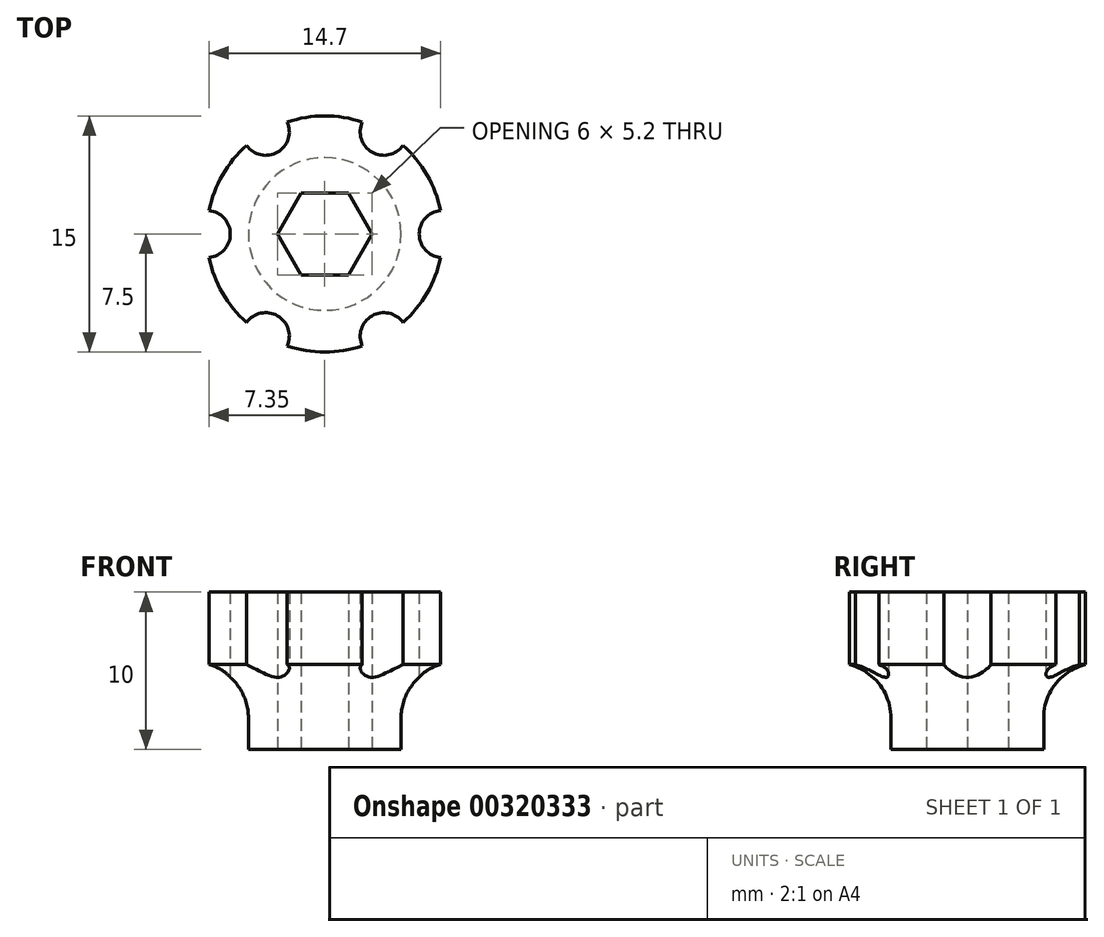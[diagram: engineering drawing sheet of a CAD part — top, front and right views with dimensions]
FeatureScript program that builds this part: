
annotation { "Feature Type Name" : "Feature", "Feature Type Description" : "" }
export const myFeature = defineFeature(function(context is Context, id is Id, definition is map)
    precondition{}
    {
        {
            var Q0;
            Q0=qCreatedBy(makeId("Top.planeOp"),FACE);
            var sketch = newSketch(context, id + "F0", { "sketchPlane" : qUnion([Q0])});
            skArc(sketch, "E0", {"start": v(-7.35, -1.5) * mm, "mid": v(-6.5, -3.75) * mm, "end": v(-4.97, -5.62) * mm});
            skArc(sketch, "E1", {"start": v(-7.35, -1.5) * mm, "mid": v(-6, 0) * mm, "end": v(-7.35, 1.5) * mm});
            skArc(sketch, "E2.1.0", {"start": v(-2.38, -7.11) * mm, "mid": v(-3, -5.2) * mm, "end": v(-4.97, -5.62) * mm});
            skArc(sketch, "E2.2.0", {"start": v(4.97, -5.62) * mm, "mid": v(3, -5.2) * mm, "end": v(2.38, -7.11) * mm});
            skArc(sketch, "E2.3.0", {"start": v(7.35, 1.5) * mm, "mid": v(6, 0) * mm, "end": v(7.35, -1.5) * mm});
            skArc(sketch, "E2.4.0", {"start": v(2.38, 7.11) * mm, "mid": v(3, 5.2) * mm, "end": v(4.97, 5.62) * mm});
            skArc(sketch, "E2.5.0", {"start": v(-4.97, 5.62) * mm, "mid": v(-3, 5.2) * mm, "end": v(-2.38, 7.11) * mm});
            skArc(sketch, "E3.trimOffspring", {"start": v(-2.38, -7.11) * mm, "mid": v(0, -7.5) * mm, "end": v(2.38, -7.11) * mm});
            skArc(sketch, "E4.trimOffspring", {"start": v(4.97, -5.62) * mm, "mid": v(6.5, -3.75) * mm, "end": v(7.35, -1.5) * mm});
            skArc(sketch, "E5.trimOffspring", {"start": v(7.35, 1.5) * mm, "mid": v(6.5, 3.75) * mm, "end": v(4.97, 5.62) * mm});
            skArc(sketch, "E6.trimOffspring", {"start": v(2.38, 7.11) * mm, "mid": v(0, 7.5) * mm, "end": v(-2.38, 7.11) * mm});
            skArc(sketch, "E7.trimOffspring", {"start": v(-4.97, 5.62) * mm, "mid": v(-6.5, 3.75) * mm, "end": v(-7.35, 1.5) * mm});
            skCircle(sketch, "E8.cCircle", {"center": v(0, 0) * mm, "radius": 2.6 * mm, "construction": true});
            skLineSegment(sketch, "E8.0", {"start": v(-1.5, 2.6) * mm, "end": v(1.5, 2.6) * mm});
            skLineSegment(sketch, "E8.1", {"start": v(1.5, 2.6) * mm, "end": v(3, 0) * mm});
            skLineSegment(sketch, "E8.2", {"start": v(3, 0) * mm, "end": v(1.5, -2.6) * mm});
            skLineSegment(sketch, "E8.3", {"start": v(1.5, -2.6) * mm, "end": v(-1.5, -2.6) * mm});
            skLineSegment(sketch, "E8.4", {"start": v(-1.5, -2.6) * mm, "end": v(-3, 0) * mm});
            skLineSegment(sketch, "E8.5", {"start": v(-3, 0) * mm, "end": v(-1.5, 2.6) * mm});
            skPoint(sketch, "E8.0.midPoint", {"position": v(0, 2.6) * mm});
            skSolve(sketch);
        }
        {
            var Q0;
            Q0=makeQuery(id+"F0.imprint","IMPRINT",FACE,{"disambiguationData":[TD([[makeQuery(id+"F0.imprint","IMPRINT",EDGE,{"derivedFrom":sQuery(id+"F0.wireOp",EDGE,"E0")}),1.0]])]});
            extrude(context, id + "F1", {"entities" : qUnion([Q0]), "depth" : 10 * mm});
        }
        {
            var Q0;
            Q0=qCreatedBy(makeId("Front.planeOp"),FACE);
            var sketch = newSketch(context, id + "F2", { "sketchPlane" : qUnion([Q0])});
            skLineSegment(sketch, "E9", {"start": v(4.85, 0) * mm, "end": v(4.85, 2) * mm});
            skArc(sketch, "E10", {"start": v(9.92, 5.13) * mm, "mid": v(6.51, 4.98) * mm, "end": v(4.85, 2) * mm});
            skLineSegment(sketch, "E11", {"start": v(4.85, 0) * mm, "end": v(9.85, 0) * mm});
            skLineSegment(sketch, "E12", {"start": v(9.85, 0) * mm, "end": v(9.92, 5.13) * mm});
            skLineSegment(sketch, "E13", {"start": v(0, 10) * mm, "end": v(0, 0) * mm});
            skLineSegment(sketch, "E14", {"start": v(0, 0) * mm, "end": v(0, 6.9) * mm, "construction": true});
            skSolve(sketch);
        }
        {
            var Q0;
            Q0 = qSketchRegion(id + "F2", true);
            var Q1;
            Q1=sQuery(id+"F2.wireOp",EDGE,"E13");
            revolve(context, id + "F3", {"operationType" : NewBodyOperationType.REMOVE, "entities" : qUnion([Q0]), "axis" : qUnion([Q1]), "revolveType" : RevolveType.ONE_DIRECTION, "oppositeDirection" : true, "angle" : 360 * degree});
        }
    });
